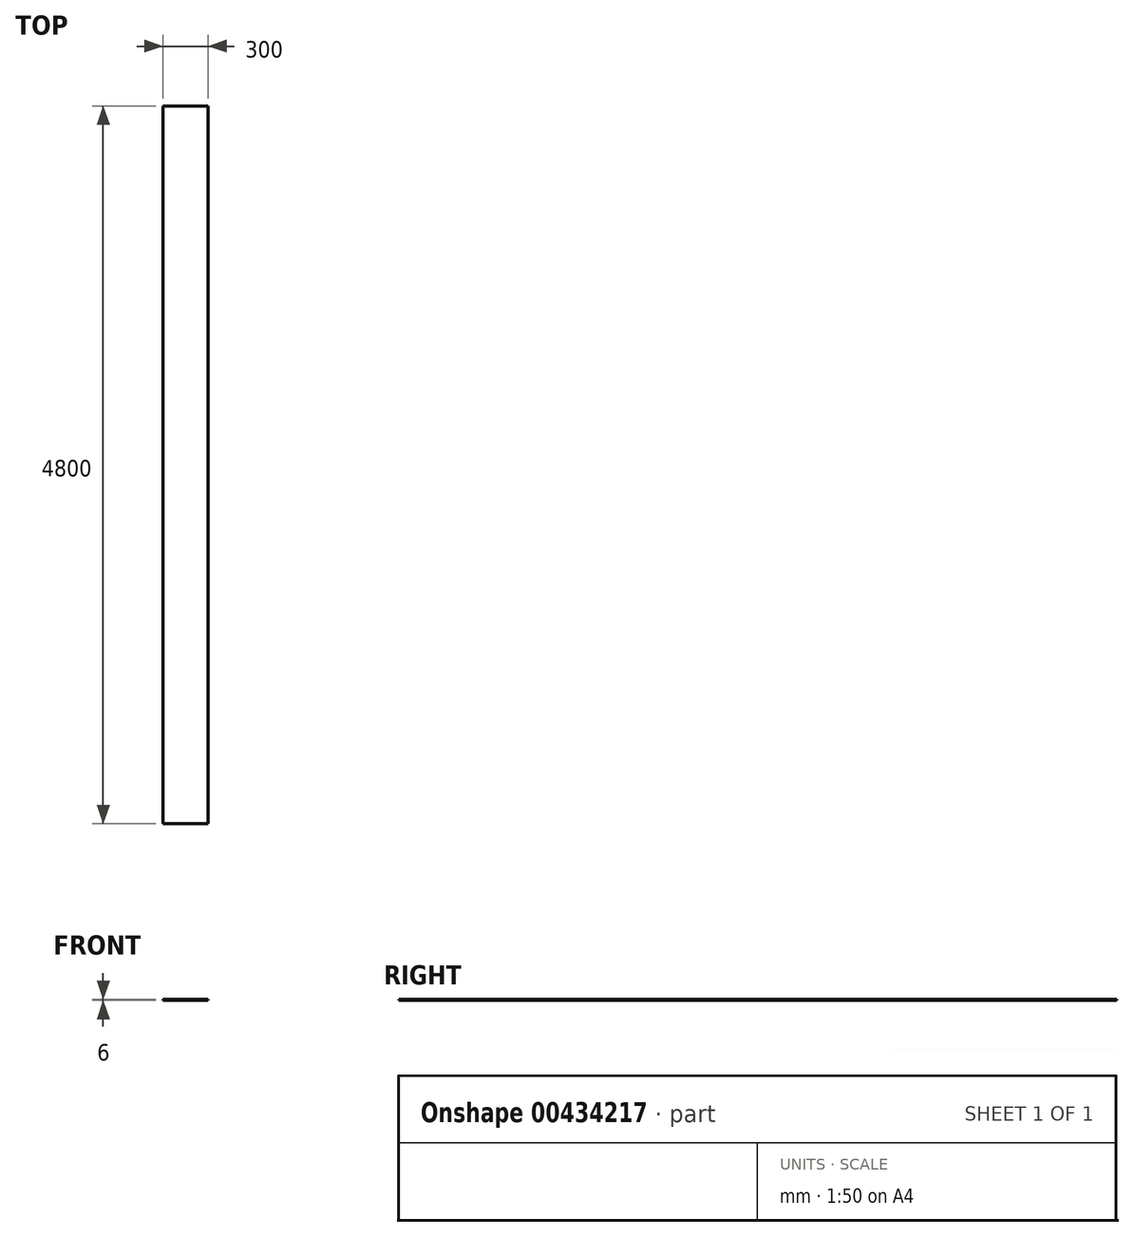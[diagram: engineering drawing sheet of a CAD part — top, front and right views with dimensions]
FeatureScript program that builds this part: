
annotation { "Feature Type Name" : "Feature", "Feature Type Description" : "" }
export const myFeature = defineFeature(function(context is Context, id is Id, definition is map)
    precondition{}
    {
        {
            var Q0;
            Q0=qCreatedBy(makeId("Right.planeOp"),FACE);
            var sketch = newSketch(context, id + "F0", { "sketchPlane" : qUnion([Q0])});
            skLineSegment(sketch, "E0", {"start": v(-2400, 0) * mm, "end": v(2400, 0) * mm});
            skLineSegment(sketch, "E1", {"start": v(-2400, 0) * mm, "end": v(-2400, -6) * mm});
            skLineSegment(sketch, "E2", {"start": v(2400, 0) * mm, "end": v(2400, -6) * mm});
            skLineSegment(sketch, "E3", {"start": v(2400, -6) * mm, "end": v(-2400, -6) * mm});
            skPoint(sketch, "E4", {"position": v(0, -6) * mm});
            skSolve(sketch);
        }
        {
            var Q0;
            Q0=makeQuery(id+"F0.imprint","IMPRINT",FACE,{"disambiguationData":[TD([[makeQuery(id+"F0.imprint","IMPRINT",EDGE,{"derivedFrom":sQuery(id+"F0.wireOp",EDGE,"E0")}),-1.0]])]});
            extrude(context, id + "F1", {"entities" : qUnion([Q0]), "oppositeDirection" : true, "depth" : 300 * mm});
        }
    });
